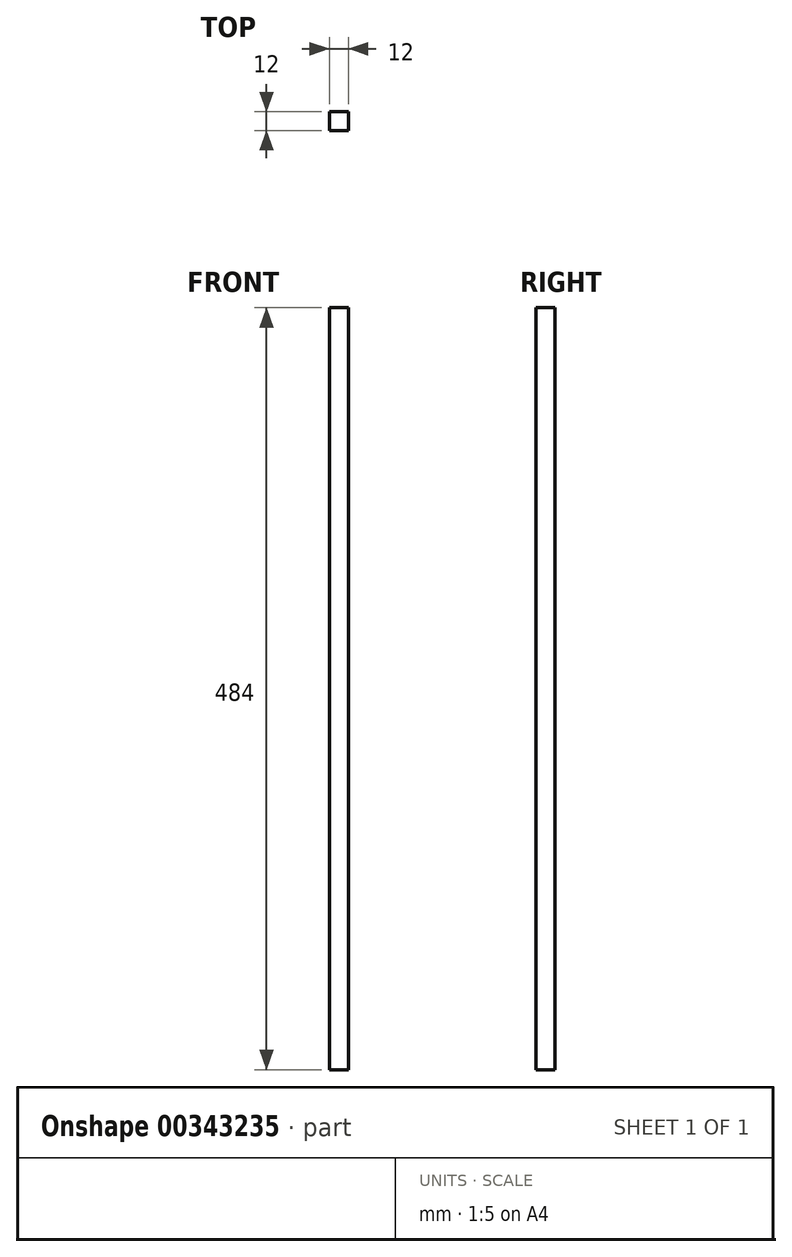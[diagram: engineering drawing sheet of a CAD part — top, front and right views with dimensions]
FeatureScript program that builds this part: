
annotation { "Feature Type Name" : "Feature", "Feature Type Description" : "" }
export const myFeature = defineFeature(function(context is Context, id is Id, definition is map)
    precondition{}
    {
        {
            var Q0;
            Q0=qCreatedBy(makeId("Top.planeOp"),FACE);
            var sketch = newSketch(context, id + "F0", { "sketchPlane" : qUnion([Q0])});
            skLineSegment(sketch, "E0.bottom", {"start": v(6, 6) * mm, "end": v(-6, 6) * mm});
            skLineSegment(sketch, "E0.top", {"start": v(6, -6) * mm, "end": v(-6, -6) * mm});
            skLineSegment(sketch, "E0.left", {"start": v(6, 6) * mm, "end": v(6, -6) * mm});
            skLineSegment(sketch, "E0.right", {"start": v(-6, 6) * mm, "end": v(-6, -6) * mm});
            skPoint(sketch, "E0.middle", {"position": v(0, 0) * mm});
            skSolve(sketch);
        }
        {
            var Q0;
            Q0=makeQuery(id+"F0.imprint","IMPRINT",FACE,{"disambiguationData":[TD([[makeQuery(id+"F0.imprint","IMPRINT",EDGE,{"derivedFrom":sQuery(id+"F0.wireOp",EDGE,"E0.bottom")}),1.0]])]});
            extrude(context, id + "F1", {"entities" : qUnion([Q0]), "depth" : 484 * mm});
        }
    });
